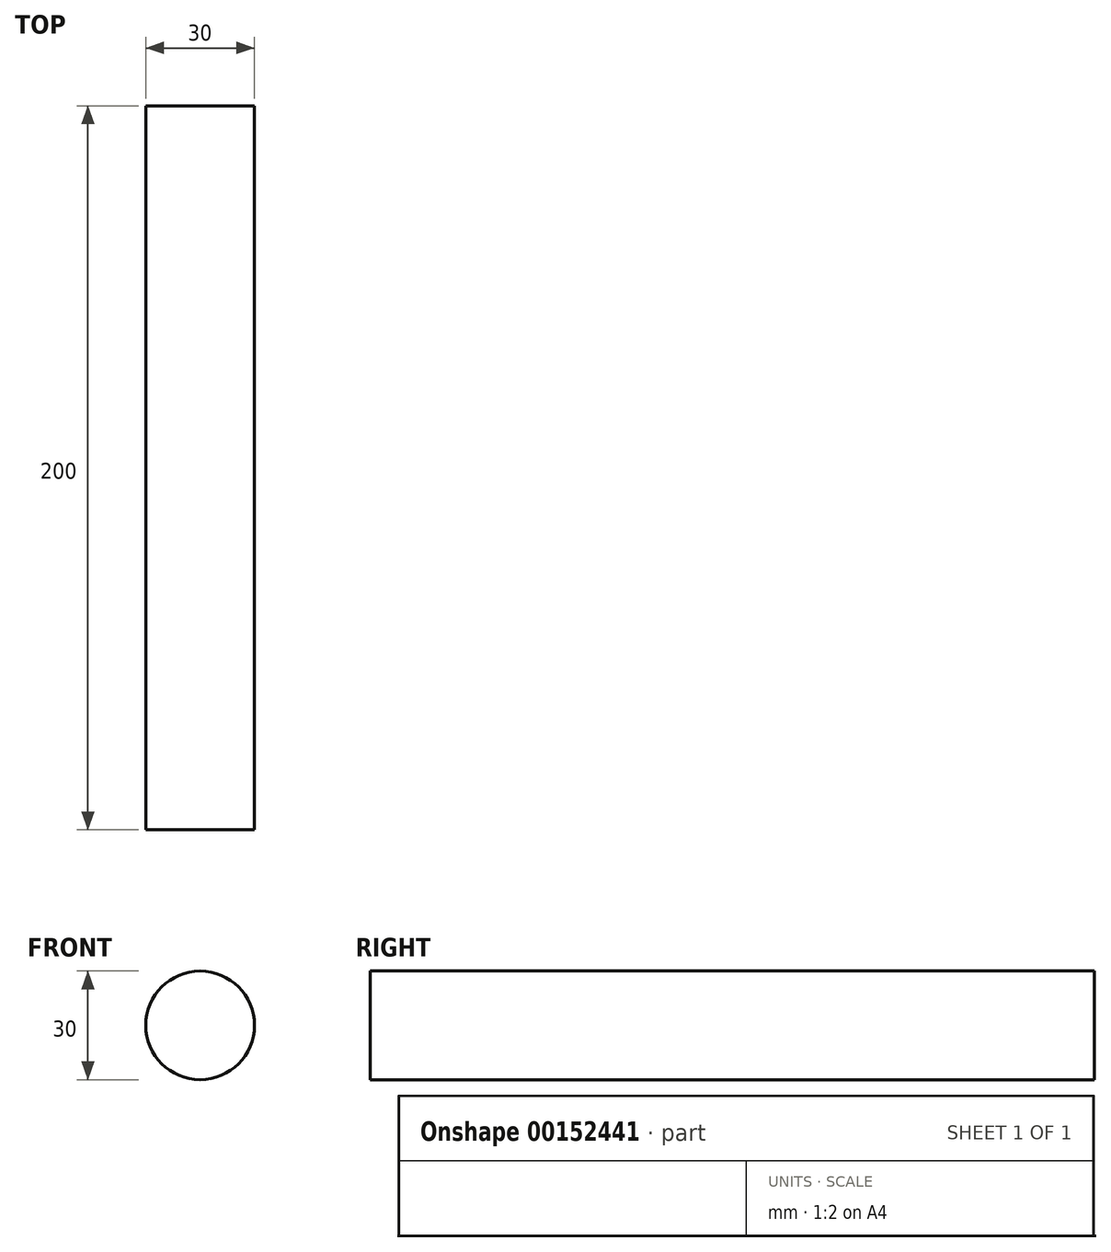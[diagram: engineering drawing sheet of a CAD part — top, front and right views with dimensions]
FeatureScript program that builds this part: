
annotation { "Feature Type Name" : "Feature", "Feature Type Description" : "" }
export const myFeature = defineFeature(function(context is Context, id is Id, definition is map)
    precondition{}
    {
        {
            var Q0;
            Q0=qCreatedBy(makeId("Front.planeOp"),FACE);
            var sketch = newSketch(context, id + "F0", { "sketchPlane" : qUnion([Q0])});
            skCircle(sketch, "E0", {"center": v(0, 0) * mm, "radius": 15 * mm});
            skSolve(sketch);
        }
        {
            var Q0;
            Q0=makeQuery(id+"F0.imprint","IMPRINT",FACE,{"disambiguationData":[TD([[makeQuery(id+"F0.imprint","IMPRINT",EDGE,{"derivedFrom":sQuery(id+"F0.wireOp",EDGE,"E0")}),1.0]])]});
            extrude(context, id + "F1", {"entities" : qUnion([Q0]), "endBound" : BoundingType.SYMMETRIC, "depth" : 200 * mm});
        }
    });
